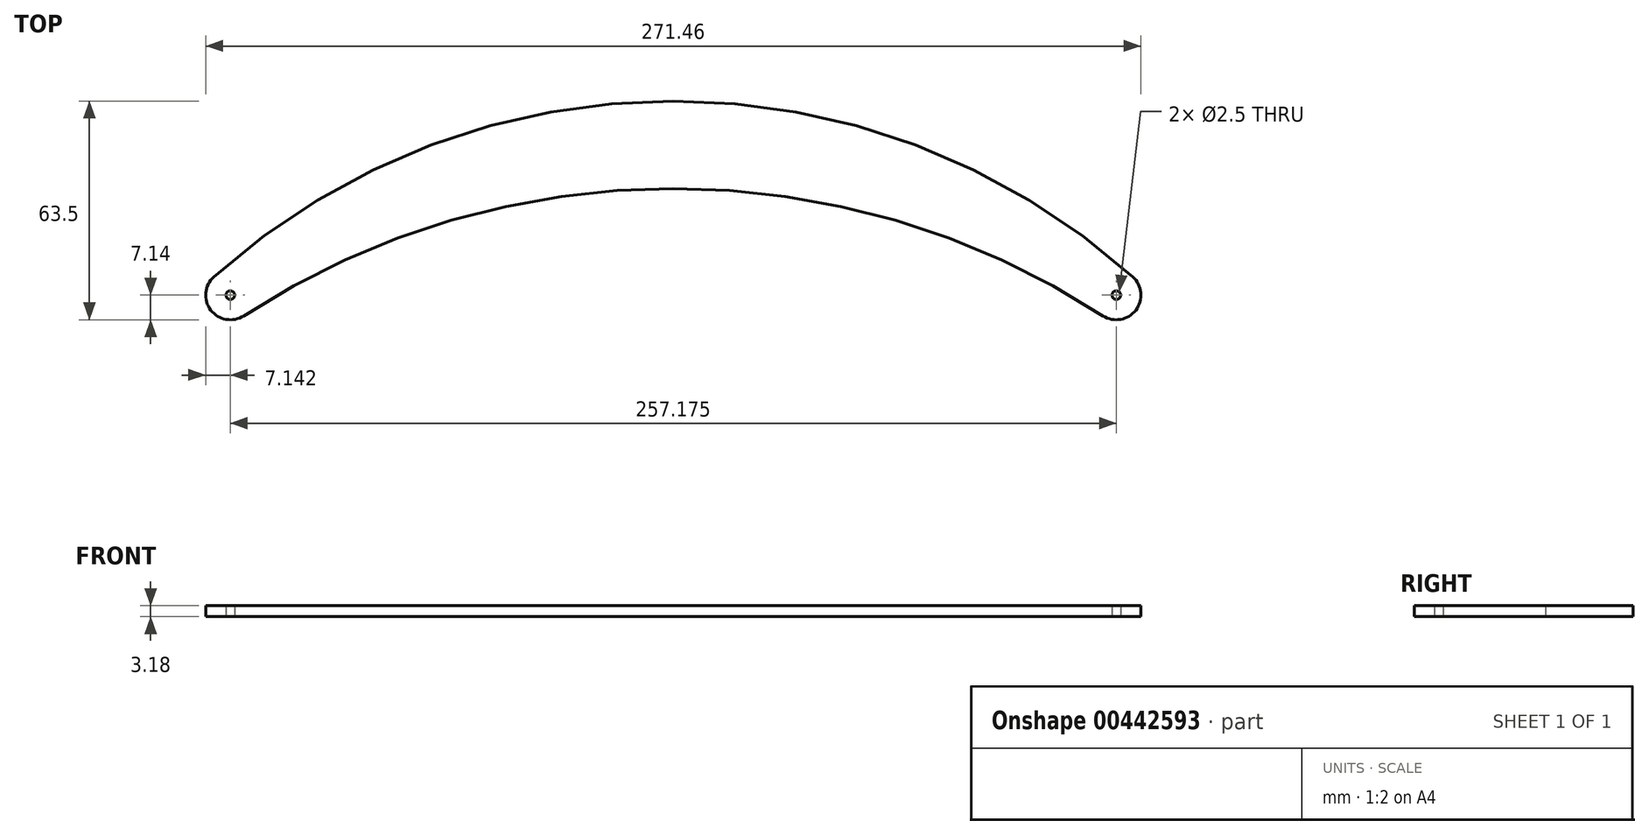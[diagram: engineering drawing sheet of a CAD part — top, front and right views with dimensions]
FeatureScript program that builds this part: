
annotation { "Feature Type Name" : "Feature", "Feature Type Description" : "" }
export const myFeature = defineFeature(function(context is Context, id is Id, definition is map)
    precondition{}
    {
        {
            var Q0;
            Q0=qCreatedBy(makeId("Top.planeOp"),FACE);
            var sketch = newSketch(context, id + "F0", { "sketchPlane" : qUnion([Q0])});
            skArc(sketch, "E0", {"start": v(-133.36, 5.32) * mm, "mid": v(-134.26, -4.34) * mm, "end": v(-124.7, -6) * mm});
            skArc(sketch, "E1", {"start": v(124.7, -6) * mm, "mid": v(134.26, -4.34) * mm, "end": v(133.36, 5.32) * mm});
            skArc(sketch, "E2", {"start": v(133.36, 5.32) * mm, "mid": v(0, 56.36) * mm, "end": v(-133.36, 5.32) * mm});
            skArc(sketch, "E3", {"start": v(124.7, -6) * mm, "mid": v(0, 30.96) * mm, "end": v(-124.7, -6) * mm});
            skLineSegment(sketch, "E4", {"start": v(-128.59, -7.14) * mm, "end": v(128.59, -7.14) * mm, "construction": true});
            skPoint(sketch, "E5", {"position": v(0, 56.36) * mm});
            skCircle(sketch, "E6", {"center": v(-128.59, 0) * mm, "radius": 1.25 * mm});
            skCircle(sketch, "E7", {"center": v(128.59, 0) * mm, "radius": 1.25 * mm});
            skSolve(sketch);
        }
        {
            var Q0;
            Q0 = qSketchRegion(id + "F0", true);
            extrude(context, id + "F1", {"entities" : qUnion([Q0]), "depth" : 3.17 * mm});
        }
    });
